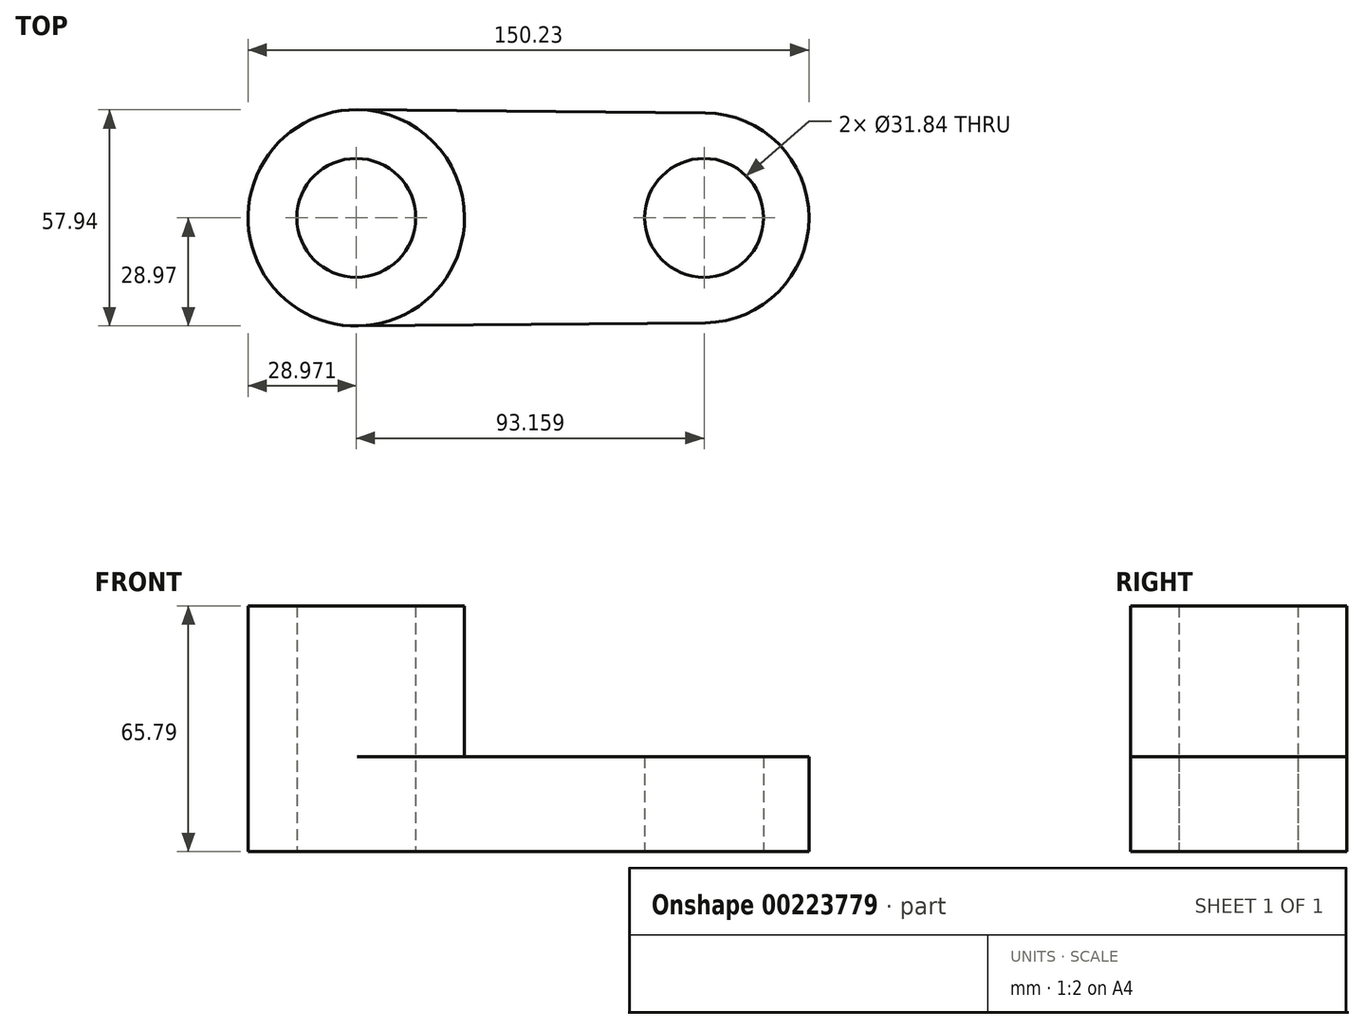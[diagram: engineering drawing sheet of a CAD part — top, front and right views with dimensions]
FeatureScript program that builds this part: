
annotation { "Feature Type Name" : "Feature", "Feature Type Description" : "" }
export const myFeature = defineFeature(function(context is Context, id is Id, definition is map)
    precondition{}
    {
        {
            var Q0;
            Q0=qCreatedBy(makeId("Top.planeOp"),FACE);
            var sketch = newSketch(context, id + "F0", { "sketchPlane" : qUnion([Q0])});
            skCircle(sketch, "E0", {"center": v(-46.58, 0) * mm, "radius": 15.92 * mm});
            skCircle(sketch, "E1", {"center": v(46.58, 0) * mm, "radius": 15.92 * mm});
            skArc(sketch, "E2", {"start": v(-46.3, 28.97) * mm, "mid": v(-75.55, 0) * mm, "end": v(-46.3, -28.97) * mm});
            skArc(sketch, "E3", {"start": v(46.84, -28.1) * mm, "mid": v(74.68, 0) * mm, "end": v(46.84, 28.1) * mm});
            skLineSegment(sketch, "E4", {"start": v(-46.3, 28.97) * mm, "end": v(46.84, 28.1) * mm});
            skLineSegment(sketch, "E5", {"start": v(46.84, -28.1) * mm, "end": v(-46.3, -28.97) * mm});
            skArc(sketch, "E6", {"start": v(-46.3, -28.97) * mm, "mid": v(-17.6, 0) * mm, "end": v(-46.3, 28.97) * mm});
            skSolve(sketch);
        }
        {
            var Q0;
            Q0=makeQuery(id+"F0.imprint","IMPRINT",FACE,{"disambiguationData":[TD([[makeQuery(id+"F0.imprint","IMPRINT",EDGE,{"derivedFrom":sQuery(id+"F0.wireOp",EDGE,"E1")}),1.0]])]});
            var Q1;
            Q1=makeQuery(id+"F0.imprint","IMPRINT",FACE,{"disambiguationData":[TD([[makeQuery(id+"F0.imprint","IMPRINT",EDGE,{"derivedFrom":sQuery(id+"F0.wireOp",EDGE,"E1")}),-1.0]])]});
            var Q2;
            Q2=makeQuery(id+"F0.imprint","IMPRINT",FACE,{"disambiguationData":[TD([[makeQuery(id+"F0.imprint","IMPRINT",EDGE,{"derivedFrom":sQuery(id+"F0.wireOp",EDGE,"E0")}),-1.0]])]});
            var Q3;
            Q3=makeQuery(id+"F0.imprint","IMPRINT",FACE,{"disambiguationData":[TD([[makeQuery(id+"F0.imprint","IMPRINT",EDGE,{"derivedFrom":sQuery(id+"F0.wireOp",EDGE,"E0")}),1.0]])]});
            extrude(context, id + "F1", {"entities" : qUnion([Q0, Q1, Q2, Q3]), "depth" : 25.4 * mm});
        }
        {
            var Q0;
            Q0=makeQuery(id+"F0.imprint","IMPRINT",FACE,{"disambiguationData":[TD([[makeQuery(id+"F0.imprint","IMPRINT",EDGE,{"derivedFrom":sQuery(id+"F0.wireOp",EDGE,"E0")}),-1.0]])]});
            var Q1;
            Q1=makeQuery(id+"F0.imprint","IMPRINT",FACE,{"disambiguationData":[TD([[makeQuery(id+"F0.imprint","IMPRINT",EDGE,{"derivedFrom":sQuery(id+"F0.wireOp",EDGE,"E0")}),1.0]])]});
            extrude(context, id + "F2", {"entities" : qUnion([Q0, Q1]), "operationType" : NewBodyOperationType.ADD, "depth" : 65.8 * mm});
        }
        {
            var Q0;
            Q0=makeQuery(id+"F0.imprint","IMPRINT",FACE,{"disambiguationData":[TD([[makeQuery(id+"F0.imprint","IMPRINT",EDGE,{"derivedFrom":sQuery(id+"F0.wireOp",EDGE,"E0")}),1.0]])]});
            extrude(context, id + "F3", {"entities" : qUnion([Q0]), "operationType" : NewBodyOperationType.REMOVE, "depth" : 76.2 * mm});
        }
        {
            var Q0;
            Q0=makeQuery(id+"F0.imprint","IMPRINT",FACE,{"disambiguationData":[TD([[makeQuery(id+"F0.imprint","IMPRINT",EDGE,{"derivedFrom":sQuery(id+"F0.wireOp",EDGE,"E1")}),1.0]])]});
            extrude(context, id + "F4", {"entities" : qUnion([Q0]), "operationType" : NewBodyOperationType.REMOVE, "depth" : 61.2 * mm});
        }
    });
